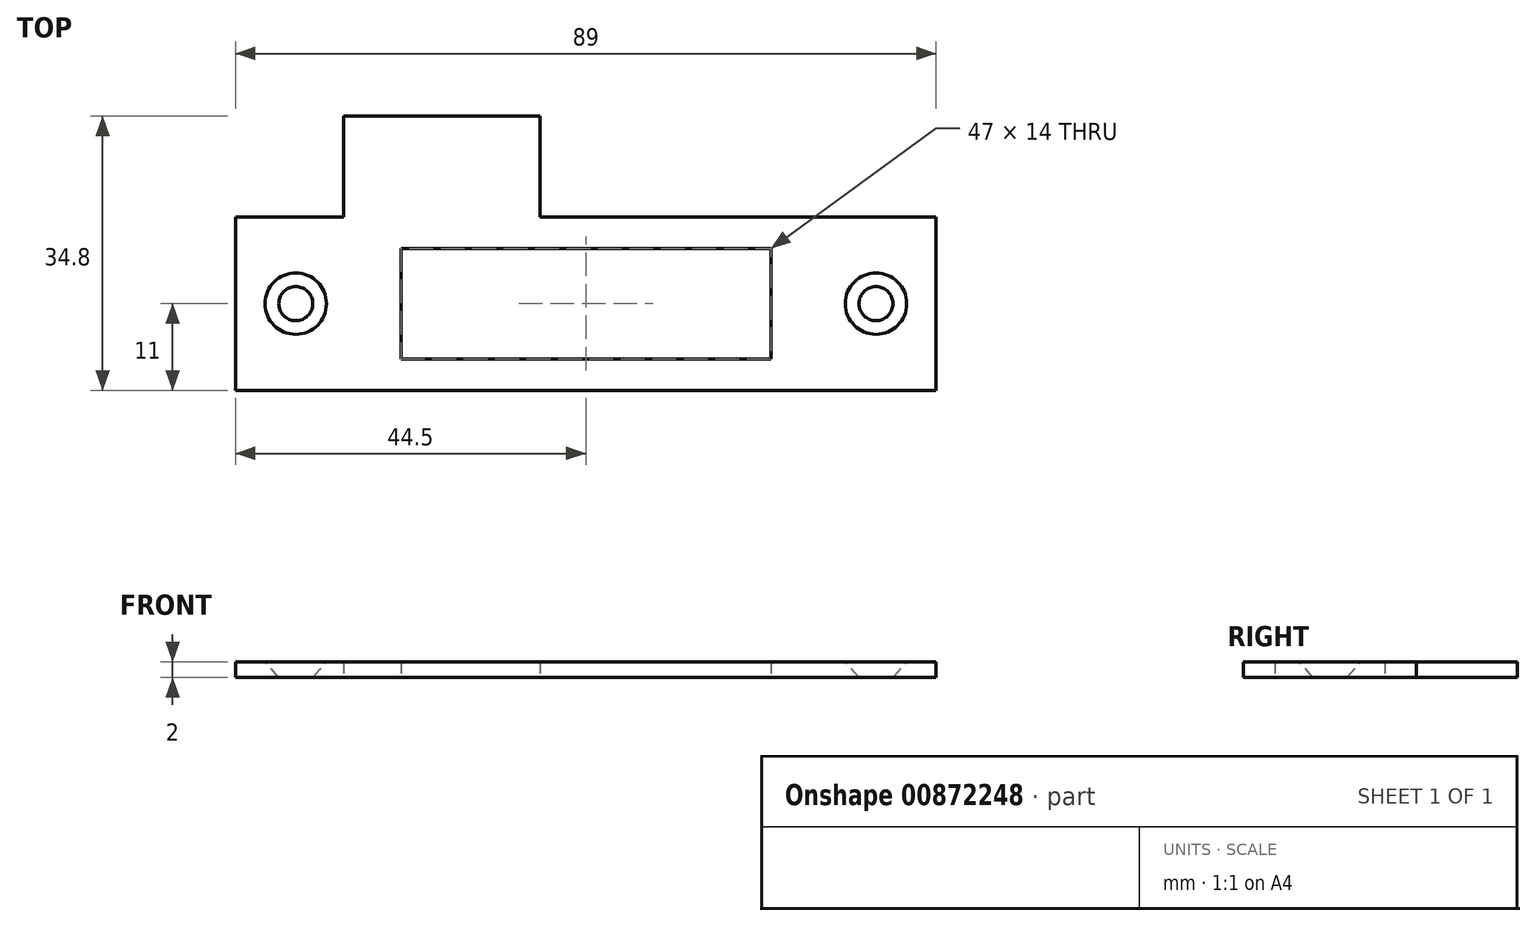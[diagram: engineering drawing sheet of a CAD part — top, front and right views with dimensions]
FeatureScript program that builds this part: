
annotation { "Feature Type Name" : "Feature", "Feature Type Description" : "" }
export const myFeature = defineFeature(function(context is Context, id is Id, definition is map)
    precondition{}
    {
        {
            var Q0;
            Q0=qCreatedBy(makeId("Top.planeOp"),FACE);
            var sketch = newSketch(context, id + "F0", { "sketchPlane" : qUnion([Q0])});
            skLineSegment(sketch, "E0.bottom", {"start": v(-44.5, -11) * mm, "end": v(44.5, -11) * mm});
            skLineSegment(sketch, "E0.top", {"start": v(-44.5, 11) * mm, "end": v(44.5, 11) * mm});
            skLineSegment(sketch, "E0.left", {"start": v(-44.5, -11) * mm, "end": v(-44.5, 11) * mm});
            skLineSegment(sketch, "E0.right", {"start": v(44.5, -11) * mm, "end": v(44.5, 11) * mm});
            skPoint(sketch, "E1", {"position": v(-44.5, 0) * mm});
            skPoint(sketch, "E2", {"position": v(0, -11) * mm});
            skCircle(sketch, "E3", {"center": v(-36.85, 0) * mm, "radius": 3.85 * mm, "construction": true});
            skCircle(sketch, "E4", {"center": v(36.85, 0) * mm, "radius": 3.85 * mm, "construction": true});
            skPoint(sketch, "E5", {"position": v(-40.7, 0) * mm});
            skPoint(sketch, "E6", {"position": v(40.7, 0) * mm});
            skLineSegment(sketch, "E7", {"start": v(-40.7, 0) * mm, "end": v(40.7, 0) * mm, "construction": true});
            skPoint(sketch, "E8", {"position": v(0, 0) * mm});
            skLineSegment(sketch, "E9.bottom", {"start": v(-23.5, -7) * mm, "end": v(23.5, -7) * mm});
            skLineSegment(sketch, "E9.top", {"start": v(-23.5, 7) * mm, "end": v(23.5, 7) * mm});
            skLineSegment(sketch, "E9.left", {"start": v(-23.5, -7) * mm, "end": v(-23.5, 7) * mm});
            skLineSegment(sketch, "E9.right", {"start": v(23.5, -7) * mm, "end": v(23.5, 7) * mm});
            skPoint(sketch, "E10", {"position": v(0, -7) * mm});
            skPoint(sketch, "E11", {"position": v(-23.5, 0) * mm});
            skLineSegment(sketch, "E12.bottom", {"start": v(-30.8, 11) * mm, "end": v(-5.8, 11) * mm});
            skLineSegment(sketch, "E12.top", {"start": v(-30.8, 23.8) * mm, "end": v(-5.8, 23.8) * mm});
            skLineSegment(sketch, "E12.left", {"start": v(-30.8, 11) * mm, "end": v(-30.8, 23.8) * mm});
            skLineSegment(sketch, "E12.right", {"start": v(-5.8, 11) * mm, "end": v(-5.8, 23.8) * mm});
            skSolve(sketch);
        }
        {
            var Q0;
            Q0=makeQuery(id+"F0.imprint","IMPRINT",FACE,{"disambiguationData":[TD([[makeQuery(id+"F0.imprint","IMPRINT",EDGE,{"derivedFrom":sQuery(id+"F0.wireOp",EDGE,"E0.bottom")}),1.0]])]});
            var Q1;
            Q1=makeQuery(id+"F0.imprint","IMPRINT",FACE,{"disambiguationData":[TD([[makeQuery(id+"F0.imprint","IMPRINT",EDGE,{"derivedFrom":sQuery(id+"F0.wireOp",EDGE,"E12.top")}),-1.0]])]});
            extrude(context, id + "F1", {"entities" : qUnion([Q0, Q1]), "depth" : 2 * mm, "offsetDistance" : 25 * mm});
        }
        {
            var Q0;
            Q0=makeQuery(id+"F1.opExtrude","CAP_FACE",FACE,{"disambiguationData":[OSD([sQuery(id+"F0.wireOp",EDGE,"E0.bottom"),sQuery(id+"F0.wireOp",EDGE,"E0.top"),sQuery(id+"F0.wireOp",EDGE,"E0.left"),sQuery(id+"F0.wireOp",EDGE,"E0.right"),sQuery(id+"F0.wireOp",EDGE,"E9.bottom"),sQuery(id+"F0.wireOp",EDGE,"E9.top"),sQuery(id+"F0.wireOp",EDGE,"E9.left"),sQuery(id+"F0.wireOp",EDGE,"E9.right"),sQuery(id+"F0.wireOp",EDGE,"E12.top"),sQuery(id+"F0.wireOp",EDGE,"E12.left"),sQuery(id+"F0.wireOp",EDGE,"E12.right")])],"isStart":false});
            var sketch = newSketch(context, id + "F2", { "sketchPlane" : qUnion([Q0])});
            skPoint(sketch, "E13.0", {"position": v(-36.85, 0) * mm});
            skPoint(sketch, "E14.0", {"position": v(36.85, 0) * mm});
            skSolve(sketch);
        }
        {
            var Q0;
            Q0=sQuery(id+"F2.wireOp",VERTEX,"E13.0");
            var Q1;
            Q1=sQuery(id+"F2.wireOp",VERTEX,"E14.0");
            var Q2;
            Q2=makeQuery(id+"F1.opExtrude","SWEPT_BODY",BODY,{"disambiguationData":[OSD([sQuery(id+"F0.wireOp",EDGE,"E0.bottom"),sQuery(id+"F0.wireOp",EDGE,"E0.top"),sQuery(id+"F0.wireOp",EDGE,"E0.left"),sQuery(id+"F0.wireOp",EDGE,"E0.right"),sQuery(id+"F0.wireOp",EDGE,"E9.bottom"),sQuery(id+"F0.wireOp",EDGE,"E9.top"),sQuery(id+"F0.wireOp",EDGE,"E9.left"),sQuery(id+"F0.wireOp",EDGE,"E9.right"),sQuery(id+"F0.wireOp",EDGE,"E12.top"),sQuery(id+"F0.wireOp",EDGE,"E12.left"),sQuery(id+"F0.wireOp",EDGE,"E12.right")])]});
            hole(context, id + "F3", {"style" : HoleStyle.C_SINK, "endStyle" : HoleEndStyle.THROUGH, "standardTappedOrClearance" : lookupTablePath({ "fit" : "Free", "standard" : "ANSI", "size" : "#6", "type" : "Clearance" }), "standardBlindInLast" : lookupTablePath({ "fit" : "Free", "standard" : "ANSI", "size" : "#6", "type" : "Clearance" }), "holeDiameter" : 3.8 * mm, "cSinkDiameter" : 7.8 * mm, "cSinkAngle" : 82 * degree, "majorDiameter" : 5 * mm, "isTappedThrough" : true, "tappedDepth" : 12 * mm, "tapClearance" : 3, "locations" : qUnion([Q0, Q1]), "scope" : qUnion([Q2])});
        }
    });
